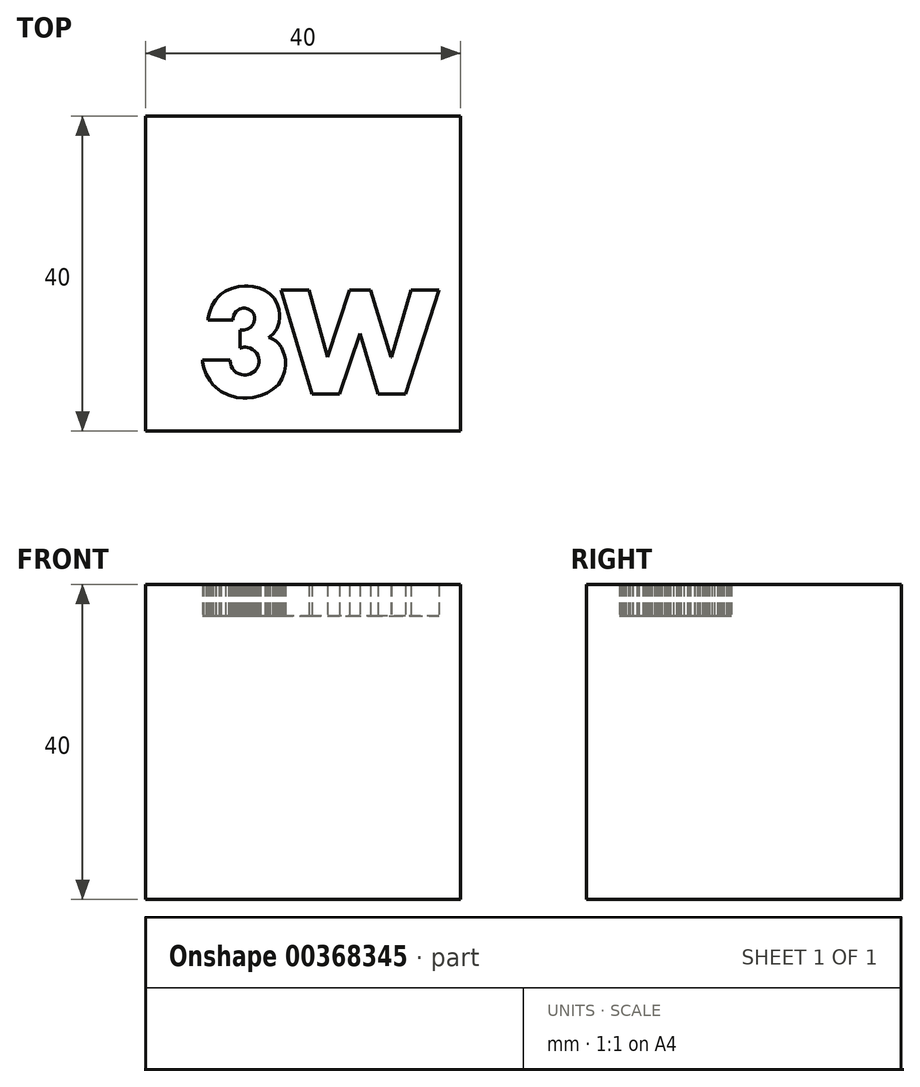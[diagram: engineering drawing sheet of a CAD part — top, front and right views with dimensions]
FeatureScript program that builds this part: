
annotation { "Feature Type Name" : "Feature", "Feature Type Description" : "" }
export const myFeature = defineFeature(function(context is Context, id is Id, definition is map)
    precondition{}
    {
        {
            var Q0;
            Q0=qCreatedBy(makeId("Top.planeOp"),FACE);
            var sketch = newSketch(context, id + "F0", { "sketchPlane" : qUnion([Q0])});
            skLineSegment(sketch, "E0", {"start": v(-20, 20) * mm, "end": v(20, 20) * mm});
            skLineSegment(sketch, "E1", {"start": v(20, 20) * mm, "end": v(20, -20) * mm});
            skLineSegment(sketch, "E2", {"start": v(20, -20) * mm, "end": v(-20, -20) * mm});
            skLineSegment(sketch, "E3", {"start": v(-20, -20) * mm, "end": v(-20, 20) * mm});
            skLineSegment(sketch, "E4", {"start": v(-12.1, -5.9) * mm, "end": v(-12.07, -5.66) * mm});
            skLineSegment(sketch, "E5", {"start": v(-12.07, -5.66) * mm, "end": v(-11.9, -4.93) * mm});
            skLineSegment(sketch, "E6", {"start": v(-11.9, -4.93) * mm, "end": v(-11.58, -4.08) * mm});
            skLineSegment(sketch, "E7", {"start": v(-11.58, -4.08) * mm, "end": v(-11.13, -3.34) * mm});
            skLineSegment(sketch, "E8", {"start": v(-11.13, -3.34) * mm, "end": v(-10.7, -2.87) * mm});
            skLineSegment(sketch, "E9", {"start": v(-10.7, -2.87) * mm, "end": v(-10.55, -2.73) * mm});
            skLineSegment(sketch, "E10", {"start": v(-10.55, -2.73) * mm, "end": v(-10.4, -2.59) * mm});
            skLineSegment(sketch, "E11", {"start": v(-10.4, -2.59) * mm, "end": v(-9.86, -2.23) * mm});
            skLineSegment(sketch, "E12", {"start": v(-9.86, -2.23) * mm, "end": v(-9.07, -1.88) * mm});
            skLineSegment(sketch, "E13", {"start": v(-9.07, -1.88) * mm, "end": v(-8.17, -1.66) * mm});
            skLineSegment(sketch, "E14", {"start": v(-8.17, -1.66) * mm, "end": v(-7.44, -1.6) * mm});
            skLineSegment(sketch, "E15", {"start": v(-7.44, -1.6) * mm, "end": v(-7.2, -1.6) * mm});
            skLineSegment(sketch, "E16", {"start": v(-7.2, -1.6) * mm, "end": v(-6.99, -1.6) * mm});
            skLineSegment(sketch, "E17", {"start": v(-6.99, -1.6) * mm, "end": v(-6.34, -1.65) * mm});
            skLineSegment(sketch, "E18", {"start": v(-6.34, -1.65) * mm, "end": v(-5.55, -1.84) * mm});
            skLineSegment(sketch, "E19", {"start": v(-5.55, -1.84) * mm, "end": v(-4.83, -2.15) * mm});
            skLineSegment(sketch, "E20", {"start": v(-4.83, -2.15) * mm, "end": v(-4.21, -2.58) * mm});
            skLineSegment(sketch, "E21", {"start": v(-4.21, -2.58) * mm, "end": v(-3.7, -3.12) * mm});
            skLineSegment(sketch, "E22", {"start": v(-3.7, -3.12) * mm, "end": v(-3.32, -3.78) * mm});
            skLineSegment(sketch, "E23", {"start": v(-3.32, -3.78) * mm, "end": v(-3.08, -4.54) * mm});
            skLineSegment(sketch, "E24", {"start": v(-3.08, -4.54) * mm, "end": v(-3, -5.2) * mm});
            skLineSegment(sketch, "E25", {"start": v(-3, -5.2) * mm, "end": v(-3, -5.42) * mm});
            skLineSegment(sketch, "E26", {"start": v(-3, -5.42) * mm, "end": v(-3, -5.61) * mm});
            skLineSegment(sketch, "E27", {"start": v(-3, -5.61) * mm, "end": v(-3.08, -6.2) * mm});
            skLineSegment(sketch, "E28", {"start": v(-3.08, -6.2) * mm, "end": v(-3.32, -6.96) * mm});
            skLineSegment(sketch, "E29", {"start": v(-3.32, -6.96) * mm, "end": v(-3.75, -7.62) * mm});
            skLineSegment(sketch, "E30", {"start": v(-3.75, -7.62) * mm, "end": v(-4.2, -8.02) * mm});
            skLineSegment(sketch, "E31", {"start": v(-4.2, -8.02) * mm, "end": v(-4.37, -8.12) * mm});
            skLineSegment(sketch, "E32", {"start": v(-4.37, -8.12) * mm, "end": v(-4.24, -8.15) * mm});
            skLineSegment(sketch, "E33", {"start": v(-4.24, -8.15) * mm, "end": v(-3.88, -8.31) * mm});
            skLineSegment(sketch, "E34", {"start": v(-3.88, -8.31) * mm, "end": v(-3.45, -8.6) * mm});
            skLineSegment(sketch, "E35", {"start": v(-3.45, -8.6) * mm, "end": v(-3.08, -8.97) * mm});
            skLineSegment(sketch, "E36", {"start": v(-3.08, -8.97) * mm, "end": v(-2.77, -9.4) * mm});
            skLineSegment(sketch, "E37", {"start": v(-2.77, -9.4) * mm, "end": v(-2.54, -9.89) * mm});
            skLineSegment(sketch, "E38", {"start": v(-2.54, -9.89) * mm, "end": v(-2.37, -10.4) * mm});
            skLineSegment(sketch, "E39", {"start": v(-2.37, -10.4) * mm, "end": v(-2.26, -10.92) * mm});
            skLineSegment(sketch, "E40", {"start": v(-2.26, -10.92) * mm, "end": v(-2.23, -11.3) * mm});
            skLineSegment(sketch, "E41", {"start": v(-2.23, -11.3) * mm, "end": v(-2.23, -11.43) * mm});
            skLineSegment(sketch, "E42", {"start": v(-2.23, -11.43) * mm, "end": v(-2.23, -11.69) * mm});
            skLineSegment(sketch, "E43", {"start": v(-2.23, -11.69) * mm, "end": v(-2.34, -12.45) * mm});
            skLineSegment(sketch, "E44", {"start": v(-2.34, -12.45) * mm, "end": v(-2.66, -13.33) * mm});
            skLineSegment(sketch, "E45", {"start": v(-2.66, -13.33) * mm, "end": v(-3.15, -14.08) * mm});
            skLineSegment(sketch, "E46", {"start": v(-3.15, -14.08) * mm, "end": v(-3.8, -14.7) * mm});
            skLineSegment(sketch, "E47", {"start": v(-3.8, -14.7) * mm, "end": v(-4.57, -15.17) * mm});
            skLineSegment(sketch, "E48", {"start": v(-4.57, -15.17) * mm, "end": v(-5.44, -15.52) * mm});
            skLineSegment(sketch, "E49", {"start": v(-5.44, -15.52) * mm, "end": v(-6.37, -15.73) * mm});
            skLineSegment(sketch, "E50", {"start": v(-6.37, -15.73) * mm, "end": v(-7.1, -15.8) * mm});
            skLineSegment(sketch, "E51", {"start": v(-7.1, -15.8) * mm, "end": v(-7.34, -15.8) * mm});
            skLineSegment(sketch, "E52", {"start": v(-7.34, -15.8) * mm, "end": v(-7.62, -15.8) * mm});
            skLineSegment(sketch, "E53", {"start": v(-7.62, -15.8) * mm, "end": v(-8.44, -15.71) * mm});
            skLineSegment(sketch, "E54", {"start": v(-8.44, -15.71) * mm, "end": v(-9.47, -15.46) * mm});
            skLineSegment(sketch, "E55", {"start": v(-9.47, -15.46) * mm, "end": v(-10.42, -15) * mm});
            skLineSegment(sketch, "E56", {"start": v(-10.42, -15) * mm, "end": v(-11.08, -14.5) * mm});
            skLineSegment(sketch, "E57", {"start": v(-11.08, -14.5) * mm, "end": v(-11.26, -14.31) * mm});
            skLineSegment(sketch, "E58", {"start": v(-11.26, -14.31) * mm, "end": v(-11.42, -14.15) * mm});
            skLineSegment(sketch, "E59", {"start": v(-11.42, -14.15) * mm, "end": v(-11.83, -13.62) * mm});
            skLineSegment(sketch, "E60", {"start": v(-11.83, -13.62) * mm, "end": v(-12.32, -12.78) * mm});
            skLineSegment(sketch, "E61", {"start": v(-12.32, -12.78) * mm, "end": v(-12.66, -11.89) * mm});
            skLineSegment(sketch, "E62", {"start": v(-12.66, -11.89) * mm, "end": v(-12.77, -11.22) * mm});
            skLineSegment(sketch, "E63", {"start": v(-12.77, -11.22) * mm, "end": v(-12.77, -11) * mm});
            skLineSegment(sketch, "E64", {"start": v(-12.77, -11) * mm, "end": v(-9.27, -11) * mm});
            skLineSegment(sketch, "E65", {"start": v(-9.27, -11) * mm, "end": v(-9.27, -11.1) * mm});
            skLineSegment(sketch, "E66", {"start": v(-9.27, -11.1) * mm, "end": v(-9.24, -11.38) * mm});
            skLineSegment(sketch, "E67", {"start": v(-9.24, -11.38) * mm, "end": v(-9.14, -11.73) * mm});
            skLineSegment(sketch, "E68", {"start": v(-9.14, -11.73) * mm, "end": v(-8.98, -12.05) * mm});
            skLineSegment(sketch, "E69", {"start": v(-8.98, -12.05) * mm, "end": v(-8.77, -12.32) * mm});
            skLineSegment(sketch, "E70", {"start": v(-8.77, -12.32) * mm, "end": v(-8.5, -12.55) * mm});
            skLineSegment(sketch, "E71", {"start": v(-8.5, -12.55) * mm, "end": v(-8.19, -12.72) * mm});
            skLineSegment(sketch, "E72", {"start": v(-8.19, -12.72) * mm, "end": v(-7.83, -12.83) * mm});
            skLineSegment(sketch, "E73", {"start": v(-7.83, -12.83) * mm, "end": v(-7.54, -12.87) * mm});
            skLineSegment(sketch, "E74", {"start": v(-7.54, -12.87) * mm, "end": v(-7.44, -12.87) * mm});
            skLineSegment(sketch, "E75", {"start": v(-7.44, -12.87) * mm, "end": v(-7.26, -12.87) * mm});
            skLineSegment(sketch, "E76", {"start": v(-7.26, -12.87) * mm, "end": v(-6.71, -12.74) * mm});
            skLineSegment(sketch, "E77", {"start": v(-6.71, -12.74) * mm, "end": v(-6.13, -12.38) * mm});
            skLineSegment(sketch, "E78", {"start": v(-6.13, -12.38) * mm, "end": v(-5.75, -11.83) * mm});
            skLineSegment(sketch, "E79", {"start": v(-5.75, -11.83) * mm, "end": v(-5.6, -11.28) * mm});
            skLineSegment(sketch, "E80", {"start": v(-5.6, -11.28) * mm, "end": v(-5.6, -11.1) * mm});
            skLineSegment(sketch, "E81", {"start": v(-5.6, -11.1) * mm, "end": v(-5.6, -11.01) * mm});
            skLineSegment(sketch, "E82", {"start": v(-5.6, -11.01) * mm, "end": v(-5.64, -10.74) * mm});
            skLineSegment(sketch, "E83", {"start": v(-5.64, -10.74) * mm, "end": v(-5.75, -10.4) * mm});
            skLineSegment(sketch, "E84", {"start": v(-5.75, -10.4) * mm, "end": v(-5.93, -10.1) * mm});
            skLineSegment(sketch, "E85", {"start": v(-5.93, -10.1) * mm, "end": v(-6.15, -9.85) * mm});
            skLineSegment(sketch, "E86", {"start": v(-6.15, -9.85) * mm, "end": v(-6.42, -9.63) * mm});
            skLineSegment(sketch, "E87", {"start": v(-6.42, -9.63) * mm, "end": v(-6.73, -9.47) * mm});
            skLineSegment(sketch, "E88", {"start": v(-6.73, -9.47) * mm, "end": v(-7.07, -9.37) * mm});
            skLineSegment(sketch, "E89", {"start": v(-7.07, -9.37) * mm, "end": v(-7.33, -9.34) * mm});
            skLineSegment(sketch, "E90", {"start": v(-7.33, -9.34) * mm, "end": v(-7.42, -9.34) * mm});
            skLineSegment(sketch, "E91", {"start": v(-7.42, -9.34) * mm, "end": v(-7.5, -9.34) * mm});
            skLineSegment(sketch, "E92", {"start": v(-7.5, -9.34) * mm, "end": v(-7.72, -9.37) * mm});
            skLineSegment(sketch, "E93", {"start": v(-7.72, -9.37) * mm, "end": v(-7.96, -9.43) * mm});
            skLineSegment(sketch, "E94", {"start": v(-7.96, -9.43) * mm, "end": v(-8.01, -9.44) * mm});
            skLineSegment(sketch, "E95", {"start": v(-8.01, -9.44) * mm, "end": v(-8.01, -7.16) * mm});
            skLineSegment(sketch, "E96", {"start": v(-8.01, -7.16) * mm, "end": v(-7.67, -7.16) * mm});
            skLineSegment(sketch, "E97", {"start": v(-7.67, -7.16) * mm, "end": v(-7.52, -7.16) * mm});
            skLineSegment(sketch, "E98", {"start": v(-7.52, -7.16) * mm, "end": v(-7.06, -7.06) * mm});
            skLineSegment(sketch, "E99", {"start": v(-7.06, -7.06) * mm, "end": v(-6.59, -6.77) * mm});
            skLineSegment(sketch, "E100", {"start": v(-6.59, -6.77) * mm, "end": v(-6.28, -6.32) * mm});
            skLineSegment(sketch, "E101", {"start": v(-6.28, -6.32) * mm, "end": v(-6.16, -5.86) * mm});
            skLineSegment(sketch, "E102", {"start": v(-6.16, -5.86) * mm, "end": v(-6.16, -5.71) * mm});
            skLineSegment(sketch, "E103", {"start": v(-6.16, -5.71) * mm, "end": v(-6.16, -5.57) * mm});
            skLineSegment(sketch, "E104", {"start": v(-6.16, -5.57) * mm, "end": v(-6.27, -5.16) * mm});
            skLineSegment(sketch, "E105", {"start": v(-6.27, -5.16) * mm, "end": v(-6.55, -4.75) * mm});
            skLineSegment(sketch, "E106", {"start": v(-6.55, -4.75) * mm, "end": v(-6.97, -4.48) * mm});
            skLineSegment(sketch, "E107", {"start": v(-6.97, -4.48) * mm, "end": v(-7.37, -4.39) * mm});
            skLineSegment(sketch, "E108", {"start": v(-7.37, -4.39) * mm, "end": v(-7.5, -4.39) * mm});
            skLineSegment(sketch, "E109", {"start": v(-7.5, -4.39) * mm, "end": v(-7.65, -4.39) * mm});
            skLineSegment(sketch, "E110", {"start": v(-7.65, -4.39) * mm, "end": v(-8.1, -4.5) * mm});
            skLineSegment(sketch, "E111", {"start": v(-8.1, -4.5) * mm, "end": v(-8.54, -4.82) * mm});
            skLineSegment(sketch, "E112", {"start": v(-8.54, -4.82) * mm, "end": v(-8.81, -5.3) * mm});
            skLineSegment(sketch, "E113", {"start": v(-8.81, -5.3) * mm, "end": v(-8.9, -5.75) * mm});
            skLineSegment(sketch, "E114", {"start": v(-8.9, -5.75) * mm, "end": v(-8.9, -5.9) * mm});
            skLineSegment(sketch, "E115", {"start": v(-8.9, -5.9) * mm, "end": v(-12.1, -5.9) * mm});
            skLineSegment(sketch, "E116", {"start": v(3.07, -10.6) * mm, "end": v(3.1, -10.6) * mm});
            skLineSegment(sketch, "E117", {"start": v(3.1, -10.6) * mm, "end": v(5.86, -2.11) * mm});
            skLineSegment(sketch, "E118", {"start": v(5.86, -2.11) * mm, "end": v(8.58, -2.11) * mm});
            skLineSegment(sketch, "E119", {"start": v(8.58, -2.11) * mm, "end": v(11.16, -10.6) * mm});
            skLineSegment(sketch, "E120", {"start": v(11.16, -10.6) * mm, "end": v(11.2, -10.6) * mm});
            skLineSegment(sketch, "E121", {"start": v(11.2, -10.6) * mm, "end": v(13.67, -2.11) * mm});
            skLineSegment(sketch, "E122", {"start": v(13.67, -2.11) * mm, "end": v(17.23, -2.11) * mm});
            skLineSegment(sketch, "E123", {"start": v(17.23, -2.11) * mm, "end": v(13.03, -15.27) * mm});
            skLineSegment(sketch, "E124", {"start": v(13.03, -15.27) * mm, "end": v(9.54, -15.27) * mm});
            skLineSegment(sketch, "E125", {"start": v(9.54, -15.27) * mm, "end": v(7.24, -7.64) * mm});
            skLineSegment(sketch, "E126", {"start": v(7.24, -7.64) * mm, "end": v(7.2, -7.64) * mm});
            skLineSegment(sketch, "E127", {"start": v(7.2, -7.64) * mm, "end": v(4.62, -15.27) * mm});
            skLineSegment(sketch, "E128", {"start": v(4.62, -15.27) * mm, "end": v(1.15, -15.27) * mm});
            skLineSegment(sketch, "E129", {"start": v(1.15, -15.27) * mm, "end": v(-2.78, -2.11) * mm});
            skLineSegment(sketch, "E130", {"start": v(-2.78, -2.11) * mm, "end": v(0.78, -2.11) * mm});
            skLineSegment(sketch, "E131", {"start": v(0.78, -2.11) * mm, "end": v(3.07, -10.6) * mm});
            skSolve(sketch);
        }
        {
            var Q0;
            Q0=makeQuery(id+"F0.imprint","IMPRINT",FACE,{"disambiguationData":[TD([[makeQuery(id+"F0.imprint","IMPRINT",EDGE,{"derivedFrom":sQuery(id+"F0.wireOp",EDGE,"E116")}),-1.0]])]});
            var Q1;
            Q1=makeQuery(id+"F0.imprint","IMPRINT",FACE,{"disambiguationData":[TD([[makeQuery(id+"F0.imprint","IMPRINT",EDGE,{"derivedFrom":sQuery(id+"F0.wireOp",EDGE,"E4")}),-1.0]])]});
            extrude(context, id + "F1", {"entities" : qUnion([Q0, Q1]), "depth" : 36 * mm});
        }
        {
            var Q0;
            Q0=makeQuery(id+"F0.imprint","IMPRINT",FACE,{"disambiguationData":[TD([[makeQuery(id+"F0.imprint","IMPRINT",EDGE,{"derivedFrom":sQuery(id+"F0.wireOp",EDGE,"E0")}),-1.0]])]});
            extrude(context, id + "F2", {"entities" : qUnion([Q0]), "operationType" : NewBodyOperationType.ADD, "depth" : 40 * mm});
        }
    });
